FCSTD DOCUMENT  (FreeCAD 0.21R33668 +26 (Git))
Label: plan cuisine3
License: All rights reserved
LicenseURL: http://en.wikipedia.org/wiki/All_rights_reserved
objects: App::FeaturePython×10, Part::Part2DObjectPython×9, App::Part×2, PartDesign::Body×1, TechDraw::DrawSVGTemplate×1, TechDraw::DrawViewImage×1, TechDraw::DrawPage×1
note: 10 computed .brp shape members not serialized (recipe doc carries the construction recipe); baked Part::Feature solids carry a one-line shape summary decoded from their .brp

FEATURE [PartDesign::Body] Body
  Origin = -> Origin
FEATURE [App::FeaturePython] Dimension  # Draft dimension (typed FeaturePython)
  Diameter = false
  Dimline = (-293,2747.46,0)
  Direction = (0,0,0)
  Distance = 4000
  End = (-2000,1844.26,0)
  Normal = (0,0,1)
  Start = (2000,1844.26,0)
FEATURE [App::FeaturePython] Dimension001  # Draft dimension (typed FeaturePython)
  Diameter = false
  Dimline = (3184,-1381.54,0)
  Direction = (0,0,0)
  Distance = 3500
  End = (2000,-1648.16,0)
  Normal = (0,0,1)
  Start = (2000,1851.84,0)
FEATURE [App::FeaturePython] Dimension002  # Draft dimension (typed FeaturePython)
  Diameter = false
  Dimline = (-3069,1346.46,0)
  Direction = (0,0,0)
  Distance = 1200
  End = (-2000,644.259,0)
  Normal = (0,0,1)
  Start = (-2000,1844.26,0)
FEATURE [App::FeaturePython] Dimension003  # Draft dimension (typed FeaturePython)
  Diameter = false
  Dimline = (-3069,-266.536,0)
  Direction = (0,0,0)
  Distance = 1100
  End = (-2000,-555.741,0)
  Normal = (0,0,1)
  Start = (-2000,-1655.74,0)
FEATURE [App::FeaturePython] Dimension004  # Draft dimension (typed FeaturePython)
  Diameter = false
  Dimline = (2632,1414.46,0)
  Direction = (0,0,0)
  Distance = 1370
  End = (2000,1844.26,0)
  Normal = (0,0,1)
  Start = (2000,474.259,0)
FEATURE [App::FeaturePython] Dimension005  # Draft dimension (typed FeaturePython)
  Diameter = false
  Dimline = (2671,-794.536,0)
  Direction = (0,0,0)
  Distance = 1400
  End = (2000,-1655.74,0)
  Normal = (0,0,1)
  Start = (2000,-255.741,0)
FEATURE [App::FeaturePython] Text  # WARN: FeaturePython — macro-defined, semantics opaque (R4)
  Placement = pos=(-1940,-1597.5,0) rot=(0,0,1;0rad)
  Text = arrivee/evacuation eau
FEATURE [App::FeaturePython] Dimension006  # Draft dimension (typed FeaturePython)
  Diameter = false
  Dimline = (1693,-2408.54,0)
  Direction = (0,0,0)
  Distance = 1984.72
  End = (2000,-1648.16,0)
  Normal = (0,0,1)
  Start = (15.2863,-1644.16,0)
FEATURE [App::FeaturePython] Text001  # WARN: FeaturePython — macro-defined, semantics opaque (R4)
  Placement = pos=(379,-1397.5,0) rot=(0,0,1;0rad)
  Text = Evacuation hote
FEATURE [App::FeaturePython] Text002  # WARN: FeaturePython — macro-defined, semantics opaque (R4)
  Placement = pos=(-4552,2651.5,0) rot=(0,0,1;0rad)
  Text = Machine Vaisselle | Machine Linge | Bouteille gaz | Poubelles | Chaise roulante - largeur 60 cm
FEATURE [Part::Part2DObjectPython] Line  # Draft 2D object (typed FeaturePython)
  Area = 0
  ChamferSize = 0
  Closed = false
  End = (363,-1392.54,0)
  FilletRadius = 0
  Length = 304.6
  MakeFace = true
  Placement = pos=(93,-1533.54,0) rot=(0,0,1;0rad)
  Points = (2) [(0,0,0),(270,141,0)]
  Start = (93,-1533.54,0)
  Subdivisions = 0
FEATURE [TechDraw::DrawSVGTemplate] Template
  EditableTexts = Designed_by_Name=Designed by Name; Drawing_number=Drawing number; FC-Date=Date; FC-SC=Scale; FC-SH=Sheet; FC-Title=Title; Subtitle=Subtitle; Weight=Weight
  Height = 210
  Orientation = 1
  Template = D:/Program Files/FreeCAD 0.21/data/Mod/TechDraw/Templates/A4_LandscapeTD.svg
  Width = 297
FEATURE [Part::Part2DObjectPython] Wire  # Draft 2D object (typed FeaturePython)
  Area = 1394000
  ChamferSize = 0
  Closed = true
  End = (-2200,644.259,0)
  FilletRadius = 0
  Length = 14340
  MakeFace = true
  Points = (8) [(-2200,2044.26,0),(2200,2044.26,0),(2200,474.259,0),(2000,474.259,0),(2000,1844.26,0),(-2000,1844.26,0),(-2000,644.259,0),(-2200,644.259,0)]
  Start = (-2200,2044.26,0)
  Subdivisions = 0
FEATURE [Part::Part2DObjectPython] Wire001  # Draft 2D object (typed FeaturePython)
  Area = 1.38e+06
  ChamferSize = 0
  Closed = true
  End = (-2000,-555.741,0)
  FilletRadius = 0
  Length = 14200
  MakeFace = true
  Points = (8) [(-2200,-555.741,0),(-2200,-1855.74,0),(2200,-1855.74,0),(2200,-255.741,0),(2000,-255.741,0),(2000,-1655.74,0),(-2000,-1655.74,0),(-2000,-555.741,0)]
  Start = (-2200,-555.741,0)
  Subdivisions = 0
FEATURE [Part::Part2DObjectPython] Circle  # Draft 2D object (typed FeaturePython)
  Area = 7975.68
  FirstAngle = 0
  LastAngle = 0
  MakeFace = true
  Placement = pos=(0,-1567.11,0) rot=(0,0,1;0rad)
  Radius = 50.3859
FEATURE [Part::Part2DObjectPython] Wire002  # Draft 2D object (typed FeaturePython)
  Area = 29287.1
  ChamferSize = 0
  Closed = true
  End = (2218.14,-996.477,0)
  FilletRadius = 0
  Length = 1709.41
  MakeFace = true
  Points = (4) [(2218.14,-177.533,0),(2253.9,-177.533,0),(2253.9,-996.477,0),(2218.14,-996.477,0)]
  Start = (2218.14,-177.533,0)
  Subdivisions = 0
FEATURE [Part::Part2DObjectPython] Arc001  # Draft 2D object (typed FeaturePython)
  Area = 0
  FirstAngle = -81.0785
  LastAngle = 79.836
  MakeFace = true
  Placement = pos=(-2100,50.6771,0) rot=(0,0,1;0rad)
  Radius = 607.559
FEATURE [Part::Part2DObjectPython] Line003  # Draft 2D object (typed FeaturePython)
  Area = 0
  ChamferSize = 0
  Closed = false
  End = (-2094,-573.536,0)
  FilletRadius = 0
  Length = 1215
  MakeFace = true
  Placement = pos=(-2094,641.464,0) rot=(0,0,1;0rad)
  Points = (2) [(0,0,0),(0,-1215,0)]
  Start = (-2094,641.464,0)
  Subdivisions = 0
FEATURE [Part::Part2DObjectPython] Line004  # Draft 2D object (typed FeaturePython)
  Area = 0
  ChamferSize = 0
  Closed = false
  End = (-2100,42.4952,0)
  FilletRadius = 0
  Length = 612.886
  MakeFace = true
  Placement = pos=(-1487.15,35.6981,0) rot=(0,0,1;0rad)
  Points = (2) [(0,0,0),(-612.849,6.79713,0)]
  Start = (-1487.15,35.6981,0)
  Subdivisions = 0
FEATURE [Part::Part2DObjectPython] Line005  # Draft 2D object (typed FeaturePython)
  Area = 0
  ChamferSize = 0
  Closed = false
  End = (2237,487.464,0)
  FilletRadius = 0
  Length = 664.997
  MakeFace = true
  Placement = pos=(2236.75,-177.533,0) rot=(0,0,1;0rad)
  Points = (2) [(0,0,0),(0.249268,664.997,0)]
  Start = (2236.75,-177.533,0)
  Subdivisions = 0
FEATURE [App::Part] Part  label="draft"
  Group = -> [Wire,Wire001,Circle,Wire002,Line,Arc001,Line003,Line004,Line005]
  Origin = -> Origin001
FEATURE [App::Part] Part001  label="cotes"
  Group = -> [Dimension,Dimension001,Dimension002,Dimension003,Dimension004,Dimension005,Text,Dimension006,Text001,Text002]
  Origin = -> Origin002
FEATURE [TechDraw::DrawViewImage] ActiveView
  Height = 100
  ImageFile = <userpath>/AppData/Local/Temp/FreeCAD/Cache/FreeCAD_Doc_d2cd94a5-bdcf-4b29-ae9a-3006eafd3a7f_7ce03f_514948/Pag9C89.tmp.png
  LockPosition = false
  Rotation = 0
  Scale = 2
  ScaleType = 2
  Width = 100
  X = 143.984
  Y = 133.921
FEATURE [TechDraw::DrawPage] Page
  KeepUpdated = true
  NextBalloonIndex = 1
  ProjectionType = 0
  Template = -> Template
  Views = -> [ActiveView]
